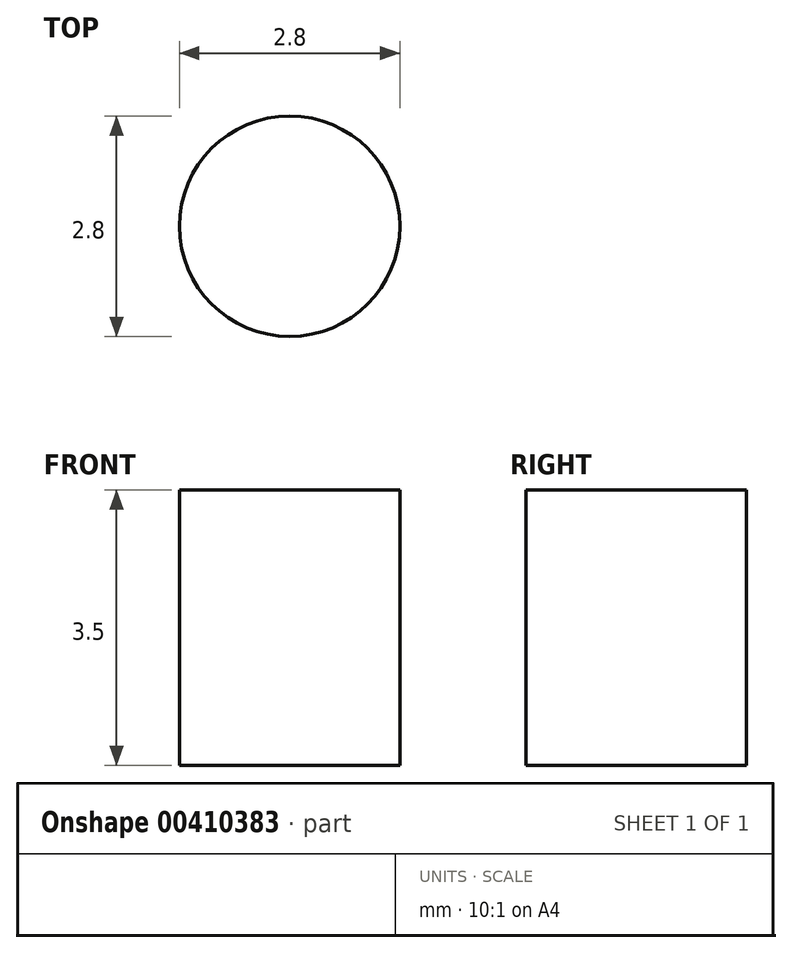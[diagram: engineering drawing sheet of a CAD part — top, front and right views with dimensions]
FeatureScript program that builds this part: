
annotation { "Feature Type Name" : "Feature", "Feature Type Description" : "" }
export const myFeature = defineFeature(function(context is Context, id is Id, definition is map)
    precondition{}
    {
        {
            var Q0;
            Q0=qCreatedBy(makeId("Top.planeOp"),FACE);
            var sketch = newSketch(context, id + "F0", { "sketchPlane" : qUnion([Q0])});
            skCircle(sketch, "E0", {"center": v(0, 0) * mm, "radius": 1.4 * mm});
            skSolve(sketch);
        }
        {
            var Q0;
            Q0 = qSketchRegion(id + "F0", true);
            extrude(context, id + "F1", {"entities" : qUnion([Q0]), "depth" : 3.5 * mm});
        }
    });
